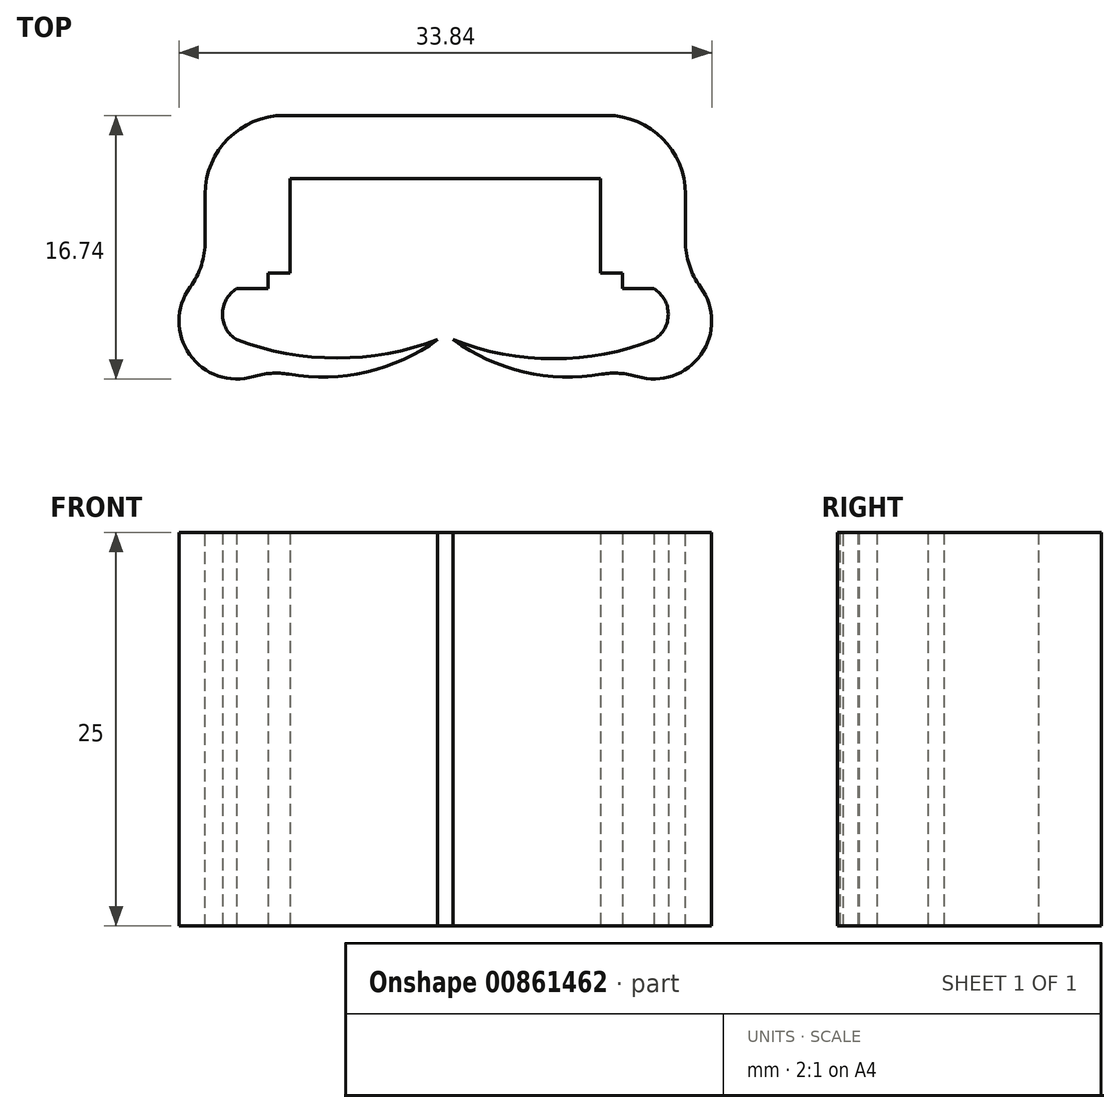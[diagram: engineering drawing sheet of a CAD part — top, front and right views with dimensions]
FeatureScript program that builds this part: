
annotation { "Feature Type Name" : "Feature", "Feature Type Description" : "" }
export const myFeature = defineFeature(function(context is Context, id is Id, definition is map)
    precondition{}
    {
        {
            var Q0;
            Q0=qCreatedBy(makeId("Top.planeOp"),FACE);
            var sketch = newSketch(context, id + "F0", { "sketchPlane" : qUnion([Q0])});
            skPoint(sketch, "E0.middle", {"position": v(0, 0) * mm});
            skLineSegment(sketch, "E1.bottom", {"start": v(11.25, 2.25) * mm, "end": v(9.85, 2.25) * mm});
            skLineSegment(sketch, "E1.top", {"start": v(11.25, 4.25) * mm, "end": v(9.85, 4.25) * mm});
            skLineSegment(sketch, "E1.left", {"start": v(11.25, 2.25) * mm, "end": v(11.25, 4.25) * mm});
            skLineSegment(sketch, "E1.right", {"start": v(9.85, 2.25) * mm, "end": v(9.85, 4.25) * mm});
            skLineSegment(sketch, "E2.bottom", {"start": v(-11.25, 2.25) * mm, "end": v(-9.85, 2.25) * mm});
            skLineSegment(sketch, "E2.top", {"start": v(-11.25, 4.25) * mm, "end": v(-9.85, 4.25) * mm});
            skLineSegment(sketch, "E2.left", {"start": v(-11.25, 2.25) * mm, "end": v(-11.25, 4.25) * mm});
            skLineSegment(sketch, "E2.right", {"start": v(-9.85, 2.25) * mm, "end": v(-9.85, 4.25) * mm});
            skLineSegment(sketch, "E3.bottom", {"start": v(11.25, 4.25) * mm, "end": v(13.25, 4.25) * mm});
            skLineSegment(sketch, "E4.bottom", {"start": v(-11.25, 4.25) * mm, "end": v(-13.25, 4.25) * mm});
            skLineSegment(sketch, "E5.top", {"start": v(-11.25, 8.25) * mm, "end": v(-9.85, 8.25) * mm});
            skLineSegment(sketch, "E5.left", {"start": v(-11.25, 4.25) * mm, "end": v(-11.25, 8.25) * mm});
            skLineSegment(sketch, "E5.right", {"start": v(-9.85, 4.25) * mm, "end": v(-9.85, 8.25) * mm});
            skLineSegment(sketch, "E6.bottom", {"start": v(9.85, 4.25) * mm, "end": v(11.25, 4.25) * mm});
            skLineSegment(sketch, "E6.top", {"start": v(9.85, 4.25) * mm, "end": v(11.25, 4.25) * mm});
            skLineSegment(sketch, "E6.left", {"start": v(9.85, 4.25) * mm, "end": v(9.85, 4.25) * mm});
            skLineSegment(sketch, "E6.right", {"start": v(11.25, 4.25) * mm, "end": v(11.25, 4.25) * mm});
            skLineSegment(sketch, "E7.bottom", {"start": v(11.25, 8.25) * mm, "end": v(9.85, 8.25) * mm});
            skLineSegment(sketch, "E7.left", {"start": v(11.25, 8.25) * mm, "end": v(11.25, 4.25) * mm});
            skLineSegment(sketch, "E7.right", {"start": v(9.85, 8.25) * mm, "end": v(9.85, 4.25) * mm});
            skLineSegment(sketch, "E8.bottom", {"start": v(-11.25, 8.25) * mm, "end": v(11.25, 8.25) * mm});
            skLineSegment(sketch, "E8.top", {"start": v(-11.25, 12.25) * mm, "end": v(11.25, 12.25) * mm});
            skLineSegment(sketch, "E8.left", {"start": v(-11.25, 8.25) * mm, "end": v(-11.25, 12.25) * mm});
            skLineSegment(sketch, "E8.right", {"start": v(11.25, 8.25) * mm, "end": v(11.25, 12.25) * mm});
            skLineSegment(sketch, "E9.bottom", {"start": v(-11.25, 12.25) * mm, "end": v(-13.25, 12.25) * mm});
            skLineSegment(sketch, "E9.left", {"start": v(-11.25, 12.25) * mm, "end": v(-11.25, 4.25) * mm});
            skLineSegment(sketch, "E9.right", {"start": v(-13.25, 12.25) * mm, "end": v(-13.25, 4.25) * mm});
            skLineSegment(sketch, "E10.bottom", {"start": v(11.25, 12.25) * mm, "end": v(13.25, 12.25) * mm});
            skLineSegment(sketch, "E10.left", {"start": v(11.25, 12.25) * mm, "end": v(11.25, 4.25) * mm});
            skLineSegment(sketch, "E10.right", {"start": v(13.25, 12.25) * mm, "end": v(13.25, 4.25) * mm});
            skLineSegment(sketch, "E11.bottom", {"start": v(-13.25, 12.25) * mm, "end": v(-13.25, 12.25) * mm});
            skLineSegment(sketch, "E12.top", {"start": v(-13.25, 12.25) * mm, "end": v(-15.25, 12.25) * mm});
            skLineSegment(sketch, "E13.bottom", {"start": v(13.25, 12.25) * mm, "end": v(15.25, 12.25) * mm});
            skArc(sketch, "E14", {"start": v(0.5, -2) * mm, "mid": v(5.66, -4.17) * mm, "end": v(11.25, -3.9) * mm});
            skArc(sketch, "E15", {"start": v(-11.25, -3.9) * mm, "mid": v(-5.66, -4.17) * mm, "end": v(-0.5, -2) * mm});
            skLineSegment(sketch, "E16", {"start": v(-11.25, 2.25) * mm, "end": v(-15.25, 2.25) * mm});
            skLineSegment(sketch, "E17", {"start": v(11.25, 2.25) * mm, "end": v(13.25, 2.25) * mm});
            skLineSegment(sketch, "E18", {"start": v(13.25, 2.25) * mm, "end": v(13.25, 4.25) * mm});
            skLineSegment(sketch, "E19", {"start": v(15.25, 4.25) * mm, "end": v(13.25, 4.25) * mm});
            skLineSegment(sketch, "E20", {"start": v(15.25, 4.25) * mm, "end": v(15.25, 12.25) * mm});
            skLineSegment(sketch, "E21", {"start": v(-15.25, 12.25) * mm, "end": v(-15.25, 4.25) * mm});
            skLineSegment(sketch, "E22", {"start": v(-13.25, 4.25) * mm, "end": v(-13.25, 2.25) * mm});
            skLineSegment(sketch, "E23", {"start": v(-13.25, 2.25) * mm, "end": v(-15.25, 2.25) * mm});
            skLineSegment(sketch, "E24", {"start": v(-15.25, 2.25) * mm, "end": v(-15.25, 4.25) * mm});
            skLineSegment(sketch, "E25", {"start": v(-13.25, 4.25) * mm, "end": v(-15.25, 4.25) * mm});
            skLineSegment(sketch, "E26", {"start": v(15.25, 4.25) * mm, "end": v(15.25, 2.25) * mm});
            skLineSegment(sketch, "E27", {"start": v(15.25, 2.25) * mm, "end": v(13.25, 2.25) * mm});
            skArc(sketch, "E28", {"start": v(-11.25, 2.25) * mm, "mid": v(-16.92, -0.82) * mm, "end": v(-11.25, -3.9) * mm});
            skArc(sketch, "E29", {"start": v(11.25, -3.9) * mm, "mid": v(16.92, -0.82) * mm, "end": v(11.25, 2.25) * mm});
            skArc(sketch, "E30", {"start": v(0.5, -2) * mm, "mid": v(6.87, -3.2) * mm, "end": v(13.25, -2) * mm});
            skArc(sketch, "E31", {"start": v(-13.25, -2) * mm, "mid": v(-6.87, -3.16) * mm, "end": v(-0.5, -2) * mm});
            skLineSegment(sketch, "E32.bottom", {"start": v(-11.25, 2.25) * mm, "end": v(-13.25, 2.25) * mm});
            skLineSegment(sketch, "E32.top", {"start": v(-11.25, 1.25) * mm, "end": v(-13.25, 1.25) * mm});
            skLineSegment(sketch, "E32.left", {"start": v(-11.25, 2.25) * mm, "end": v(-11.25, 1.25) * mm});
            skLineSegment(sketch, "E32.right", {"start": v(-13.25, 2.25) * mm, "end": v(-13.25, 1.25) * mm});
            skPoint(sketch, "E33.oppositeSnap0", {"position": v(-12.25, 1.25) * mm});
            skLineSegment(sketch, "E33.top", {"start": v(11.25, 1.25) * mm, "end": v(13.25, 1.25) * mm});
            skLineSegment(sketch, "E33.left", {"start": v(11.25, 2.25) * mm, "end": v(11.25, 1.25) * mm});
            skLineSegment(sketch, "E33.right", {"start": v(13.25, 2.25) * mm, "end": v(13.25, 1.25) * mm});
            skArc(sketch, "E34", {"start": v(-11.25, 1.25) * mm, "mid": v(-13.88, 0.62) * mm, "end": v(-13.25, -2) * mm});
            skArc(sketch, "E35", {"start": v(13.25, -2) * mm, "mid": v(13.88, 0.62) * mm, "end": v(11.25, 1.25) * mm});
            skSolve(sketch);
        }
        {
            var Q0;
            Q0 = qSketchRegion(id + "F0", true);
            extrude(context, id + "F1", {"entities" : qUnion([Q0]), "depth" : 25 * mm, "offsetDistance" : 25 * mm});
        }
        {
            var Q0;
            Q0=makeQuery(id+"F1.opExtrude","SWEPT_EDGE",EDGE,{"disambiguationData":[OSD([sQuery(id+"F0.wireOp",EDGE,"E13.bottom"),sQuery(id+"F0.wireOp",EDGE,"E20")])]});
            var Q1;
            Q1=makeQuery(id+"F1.opExtrude","SWEPT_EDGE",EDGE,{"disambiguationData":[OSD([sQuery(id+"F0.wireOp",EDGE,"E12.top"),sQuery(id+"F0.wireOp",EDGE,"E21")])]});
            fillet(context, id + "F2", {"entities" : qUnion([Q0, Q1]), "radius" : 5 * mm, "tangentPropagation" : true, "allowEdgeOverflow" : false});
        }
        {
            var Q0;
            Q0=makeQuery(id+"F1.opExtrude","SWEPT_EDGE",EDGE,{"disambiguationData":[OSD([sQuery(id+"F0.wireOp",EDGE,"E23"),sQuery(id+"F0.wireOp",EDGE,"E24"),sQuery(id+"F0.wireOp",EDGE,"E28")])]});
            var Q1;
            Q1=makeQuery(id+"F1.opExtrude","SWEPT_EDGE",EDGE,{"disambiguationData":[OSD([sQuery(id+"F0.wireOp",EDGE,"E26"),sQuery(id+"F0.wireOp",EDGE,"E27"),sQuery(id+"F0.wireOp",EDGE,"E29")])]});
            fillet(context, id + "F3", {"entities" : qUnion([Q0, Q1]), "radius" : 5 * mm, "tangentPropagation" : true, "allowEdgeOverflow" : false});
        }
        {
            var Q0;
            Q0=makeQuery(id+"F1.opExtrude","SWEPT_EDGE",EDGE,{"disambiguationData":[OSD([sQuery(id+"F0.wireOp",EDGE,"E14"),sQuery(id+"F0.wireOp",EDGE,"E29")])]});
            fillet(context, id + "F4", {"entities" : qUnion([Q0]), "radius" : 5 * mm, "tangentPropagation" : true, "allowEdgeOverflow" : false});
        }
        {
            var Q0;
            Q0=makeQuery(id+"F1.opExtrude","SWEPT_EDGE",EDGE,{"disambiguationData":[OSD([sQuery(id+"F0.wireOp",EDGE,"E15"),sQuery(id+"F0.wireOp",EDGE,"E28")])]});
            fillet(context, id + "F5", {"entities" : qUnion([Q0]), "radius" : 5 * mm, "tangentPropagation" : true, "allowEdgeOverflow" : false});
        }
    });
